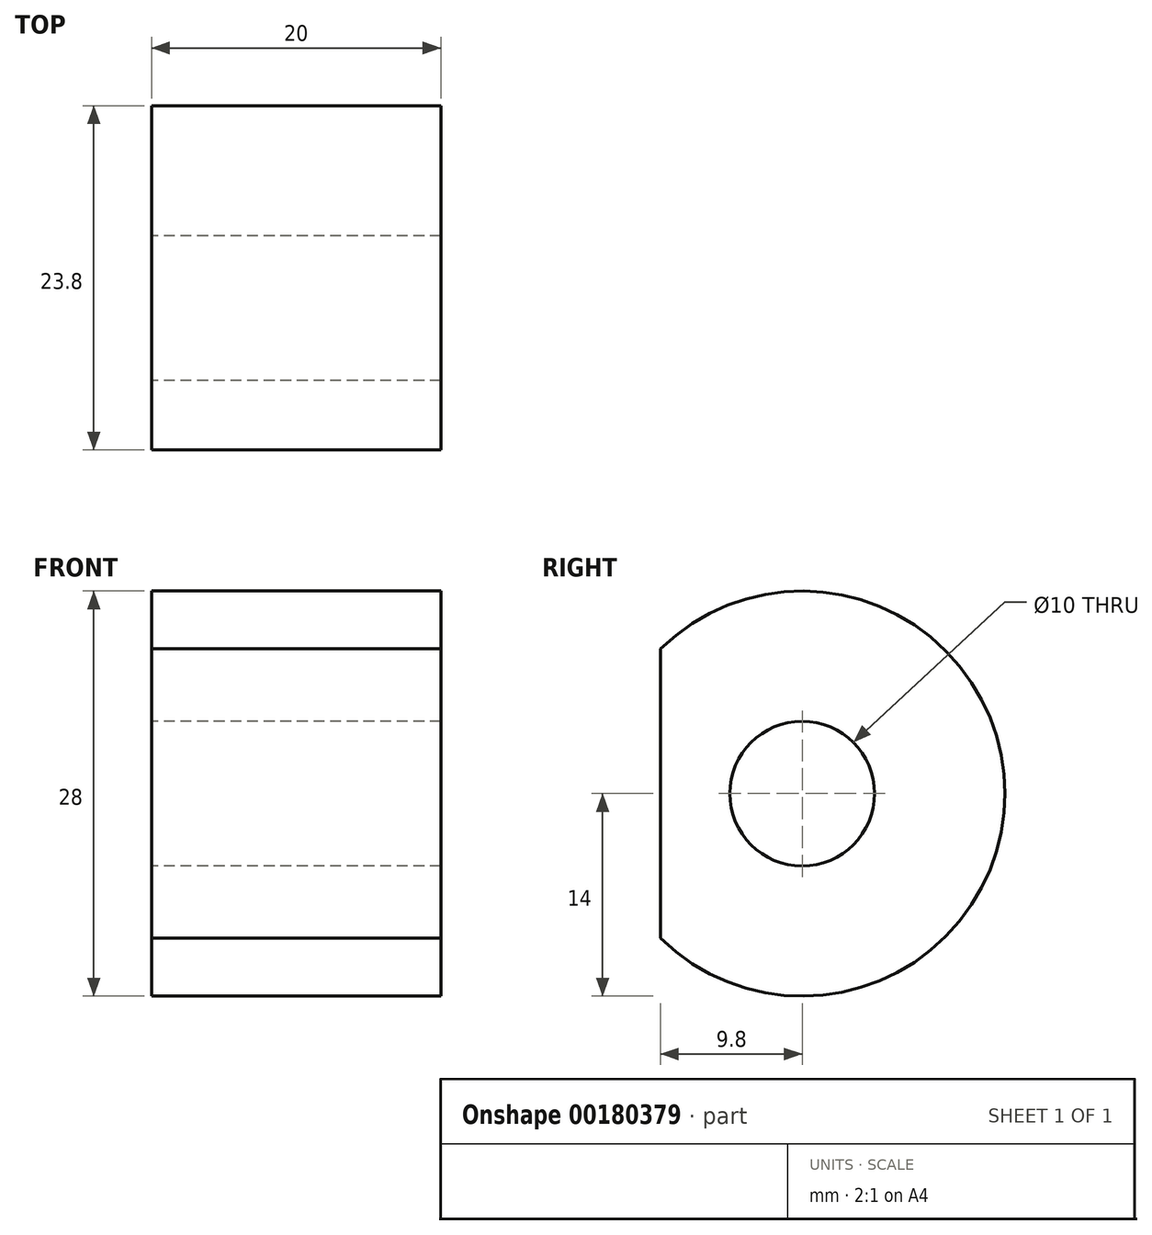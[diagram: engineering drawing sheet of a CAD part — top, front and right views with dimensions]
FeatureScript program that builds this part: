
annotation { "Feature Type Name" : "Feature", "Feature Type Description" : "" }
export const myFeature = defineFeature(function(context is Context, id is Id, definition is map)
    precondition{}
    {
        {
            var Q0;
            Q0=qCreatedBy(makeId("Right.planeOp"),FACE);
            var sketch = newSketch(context, id + "F0", { "sketchPlane" : qUnion([Q0])});
            skCircle(sketch, "E0", {"center": v(0, 0) * mm, "radius": 5 * mm});
            skLineSegment(sketch, "E1", {"start": v(0, 0) * mm, "end": v(0, 5) * mm});
            skLineSegment(sketch, "E2", {"start": v(0, 0) * mm, "end": v(0, -14) * mm});
            skArc(sketch, "E3", {"start": v(-9.8, -10) * mm, "mid": v(14, 0) * mm, "end": v(-9.8, 10) * mm});
            skLineSegment(sketch, "E4", {"start": v(0, 0) * mm, "end": v(-9.8, 0) * mm});
            skLineSegment(sketch, "E5", {"start": v(-9.8, 0) * mm, "end": v(-9.8, 10) * mm});
            skLineSegment(sketch, "E6", {"start": v(-9.8, 10) * mm, "end": v(-9.8, 0) * mm});
            skLineSegment(sketch, "E7", {"start": v(-9.8, 0) * mm, "end": v(-9.8, -10) * mm});
            skLineSegment(sketch, "E8", {"start": v(-9.8, 10) * mm, "end": v(-9.8, -10) * mm});
            skSolve(sketch);
        }
        {
            var Q0;
            Q0=qSketchRegion(id+"F0",true);
            extrude(context, id + "F1", {"entities" : qUnion([Q0]), "depth" : 20 * mm});
        }
    });
